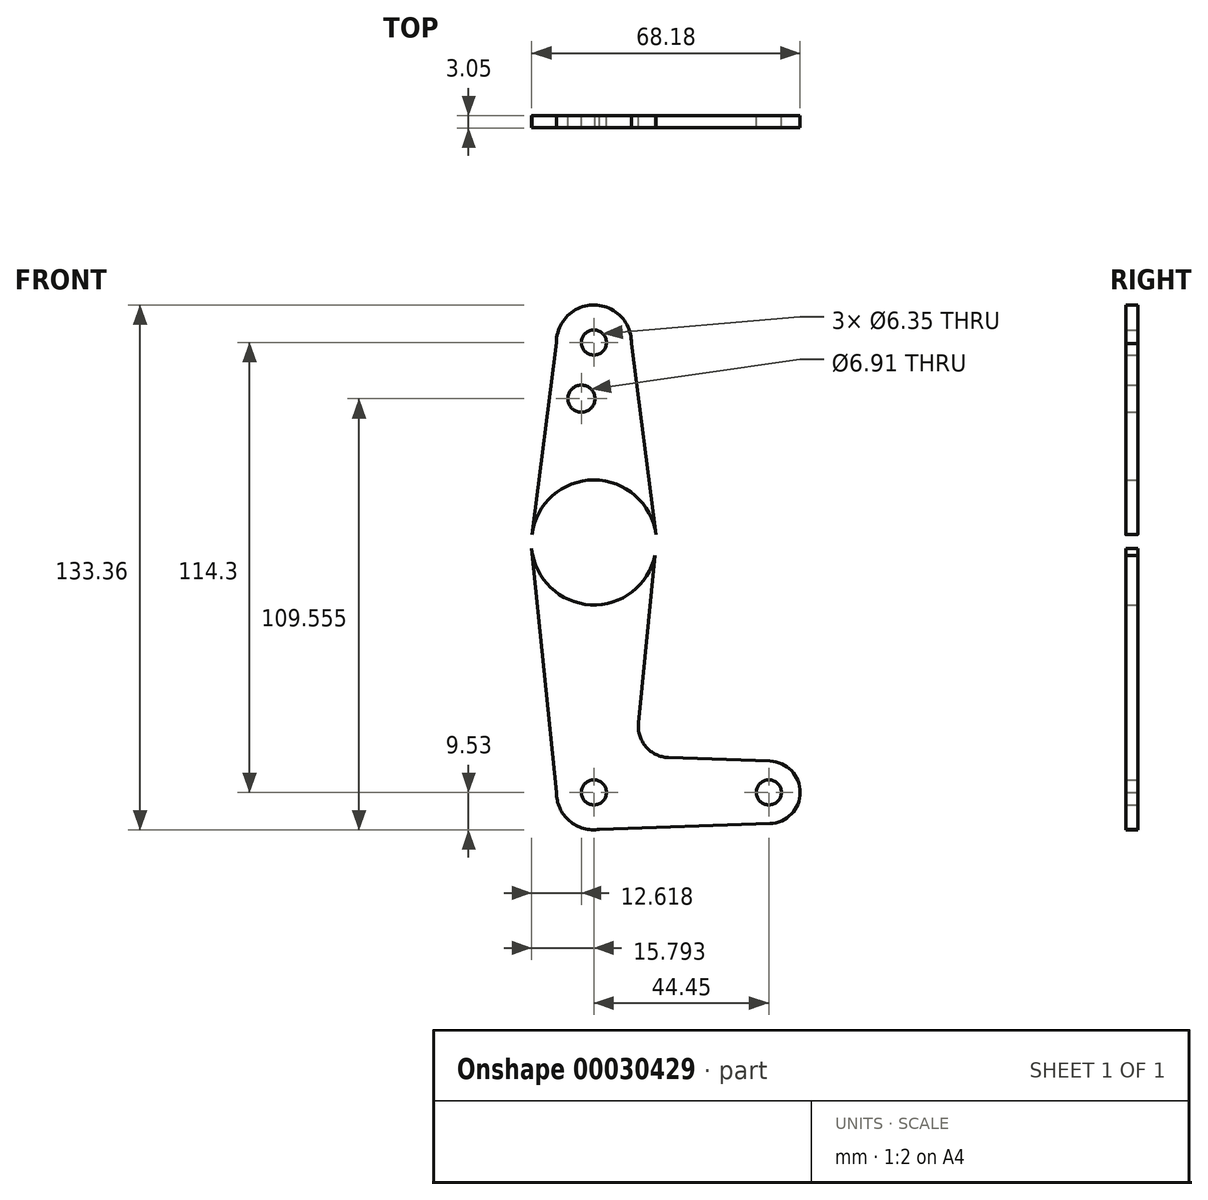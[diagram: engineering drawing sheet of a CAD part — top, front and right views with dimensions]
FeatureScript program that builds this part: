
annotation { "Feature Type Name" : "Feature", "Feature Type Description" : "" }
export const myFeature = defineFeature(function(context is Context, id is Id, definition is map)
    precondition{}
    {
        {
            var Q0;
            Q0=qCreatedBy(makeId("Front.planeOp"),FACE);
            var sketch = newSketch(context, id + "F0", { "sketchPlane" : qUnion([Q0])});
            skLineSegment(sketch, "E0", {"start": v(-1.4, 114.3) * mm, "end": v(-1.4, 0) * mm});
            skLineSegment(sketch, "E1", {"start": v(-1.4, 0) * mm, "end": v(43.04, 0) * mm});
            skCircle(sketch, "E2", {"center": v(-1.4, 114.3) * mm, "radius": 9.53 * mm});
            skCircle(sketch, "E3", {"center": v(-1.4, 63.5) * mm, "radius": 15.88 * mm});
            skCircle(sketch, "E4", {"center": v(-1.4, 0) * mm, "radius": 9.53 * mm});
            skCircle(sketch, "E5", {"center": v(43.04, 0) * mm, "radius": 7.94 * mm});
            skLineSegment(sketch, "E6", {"start": v(-10.93, 114.34) * mm, "end": v(-17.15, 65.5) * mm});
            skLineSegment(sketch, "E7", {"start": v(8.11, 113.98) * mm, "end": v(14.34, 65.52) * mm});
            skLineSegment(sketch, "E8", {"start": v(14.13, 60.22) * mm, "end": v(9.9, 17.58) * mm});
            skLineSegment(sketch, "E9", {"start": v(17.53, 8.85) * mm, "end": v(43.33, 7.93) * mm});
            skLineSegment(sketch, "E10", {"start": v(0, -9.42) * mm, "end": v(43.32, -7.93) * mm});
            skArc(sketch, "E11.filletArc", {"start": v(9.9, 17.58) * mm, "mid": v(11.83, 11.57) * mm, "end": v(17.53, 8.85) * mm});
            skCircle(sketch, "E12", {"center": v(-1.4, 114.3) * mm, "radius": 3.18 * mm});
            skCircle(sketch, "E13", {"center": v(-1.4, 63.5) * mm, "radius": 3.18 * mm});
            skCircle(sketch, "E14", {"center": v(-1.4, 0) * mm, "radius": 3.18 * mm});
            skCircle(sketch, "E15", {"center": v(43.04, 0) * mm, "radius": 3.18 * mm});
            skCircle(sketch, "E16", {"center": v(-4.58, 100.03) * mm, "radius": 3.45 * mm});
            skLineSegment(sketch, "E17", {"start": v(-10.93, 0) * mm, "end": v(-17.2, 61.91) * mm});
            skSolve(sketch);
        }
        {
            var Q0;
            {var subQ0=sQuery(id+"F0.wireOp",EDGE,"E10");Q0=makeQuery(id+"F0.imprint","IMPRINT",FACE,{"disambiguationData":[TD([[makeQuery(id+"F0.imprint","IMPRINT",EDGE,{"derivedFrom":subQ0}),1.0]])]});}
            var Q1;
            Q1=makeQuery(id+"F0.imprint","IMPRINT",FACE,{"disambiguationData":[TD([[makeQuery(id+"F0.imprint","IMPRINT",EDGE,{"derivedFrom":sQuery(id+"F0.wireOp",EDGE,"E12")}),-1.0]])]});
            var Q2;
            Q2=makeQuery(id+"F0.imprint","IMPRINT",FACE,{"disambiguationData":[TD([[makeQuery(id+"F0.imprint","IMPRINT",EDGE,{"derivedFrom":sQuery(id+"F0.wireOp",EDGE,"E15")}),-1.0]])]});
            var Q3;
            {var subQ4=sQuery(id+"F0.wireOp",EDGE,"E6");Q3=makeQuery(id+"F0.imprint","IMPRINT",FACE,{"disambiguationData":[TD([[makeQuery(id+"F0.imprint","IMPRINT",EDGE,{"derivedFrom":subQ4}),1.0]])]});}
            var Q4;
            {var subQ4=sQuery(id+"F0.wireOp",EDGE,"E7");Q4=makeQuery(id+"F0.imprint","IMPRINT",FACE,{"disambiguationData":[TD([[makeQuery(id+"F0.imprint","IMPRINT",EDGE,{"derivedFrom":subQ4}),-1.0]])]});}
            var Q5;
            {var subQ1=sQuery(id+"F0.wireOp",EDGE,"E0");var subQ4=sQuery(id+"F0.wireOp",EDGE,"E3");var subQ7=makeQuery(id+"F0.imprint","INTERSECT",VERTEX,{"disambiguationData":[OD(0.0)],"derivedFrom":[subQ1,subQ4]});Q5=makeQuery(id+"F0.imprint","IMPRINT",FACE,{"disambiguationData":[TD([[makeQuery(id+"F0.imprint","IMPRINT",EDGE,{"disambiguationData":[TD([[subQ7,-1.0]])],"derivedFrom":subQ1}),1.0]])]});}
            var Q6;
            {var subQ1=sQuery(id+"F0.wireOp",EDGE,"E0");var subQ4=sQuery(id+"F0.wireOp",EDGE,"E3");var subQ8=makeQuery(id+"F0.imprint","INTERSECT",VERTEX,{"disambiguationData":[OD(0.0)],"derivedFrom":[subQ1,subQ4]});Q6=makeQuery(id+"F0.imprint","IMPRINT",FACE,{"disambiguationData":[TD([[makeQuery(id+"F0.imprint","IMPRINT",EDGE,{"disambiguationData":[TD([[subQ8,-1.0]])],"derivedFrom":subQ1}),-1.0]])]});}
            var Q7;
            {var subQ3=sQuery(id+"F0.wireOp",EDGE,"E0");var subQ5=sQuery(id+"F0.wireOp",EDGE,"E4");var subQ9=makeQuery(id+"F0.imprint","INTERSECT",VERTEX,{"derivedFrom":[subQ3,subQ5]});Q7=makeQuery(id+"F0.imprint","IMPRINT",FACE,{"disambiguationData":[TD([[makeQuery(id+"F0.imprint","IMPRINT",EDGE,{"disambiguationData":[TD([[subQ9,-1.0]])],"derivedFrom":subQ3}),-1.0]])]});}
            var Q8;
            {var subQ1=sQuery(id+"F0.wireOp",EDGE,"E8");Q8=makeQuery(id+"F0.imprint","IMPRINT",FACE,{"disambiguationData":[TD([[makeQuery(id+"F0.imprint","IMPRINT",EDGE,{"derivedFrom":subQ1}),-1.0]])]});}
            var Q9;
            {var subQ0=sQuery(id+"F0.wireOp",EDGE,"E17");Q9=makeQuery(id+"F0.imprint","IMPRINT",FACE,{"disambiguationData":[TD([[makeQuery(id+"F0.imprint","IMPRINT",EDGE,{"derivedFrom":subQ0}),-1.0]])]});}
            var Q10;
            {var subQ3=sQuery(id+"F0.wireOp",EDGE,"E0");var subQ5=sQuery(id+"F0.wireOp",EDGE,"E4");var subQ7=makeQuery(id+"F0.imprint","INTERSECT",VERTEX,{"derivedFrom":[subQ3,subQ5]});Q10=makeQuery(id+"F0.imprint","IMPRINT",FACE,{"disambiguationData":[TD([[makeQuery(id+"F0.imprint","IMPRINT",EDGE,{"disambiguationData":[TD([[subQ7,-1.0]])],"derivedFrom":subQ3}),1.0]])]});}
            extrude(context, id + "F1", {"entities" : qUnion([Q0, Q1, Q2, Q3, Q4, Q5, Q6, Q7, Q8, Q9, Q10]), "depth" : 3.05 * mm});
        }
    });
